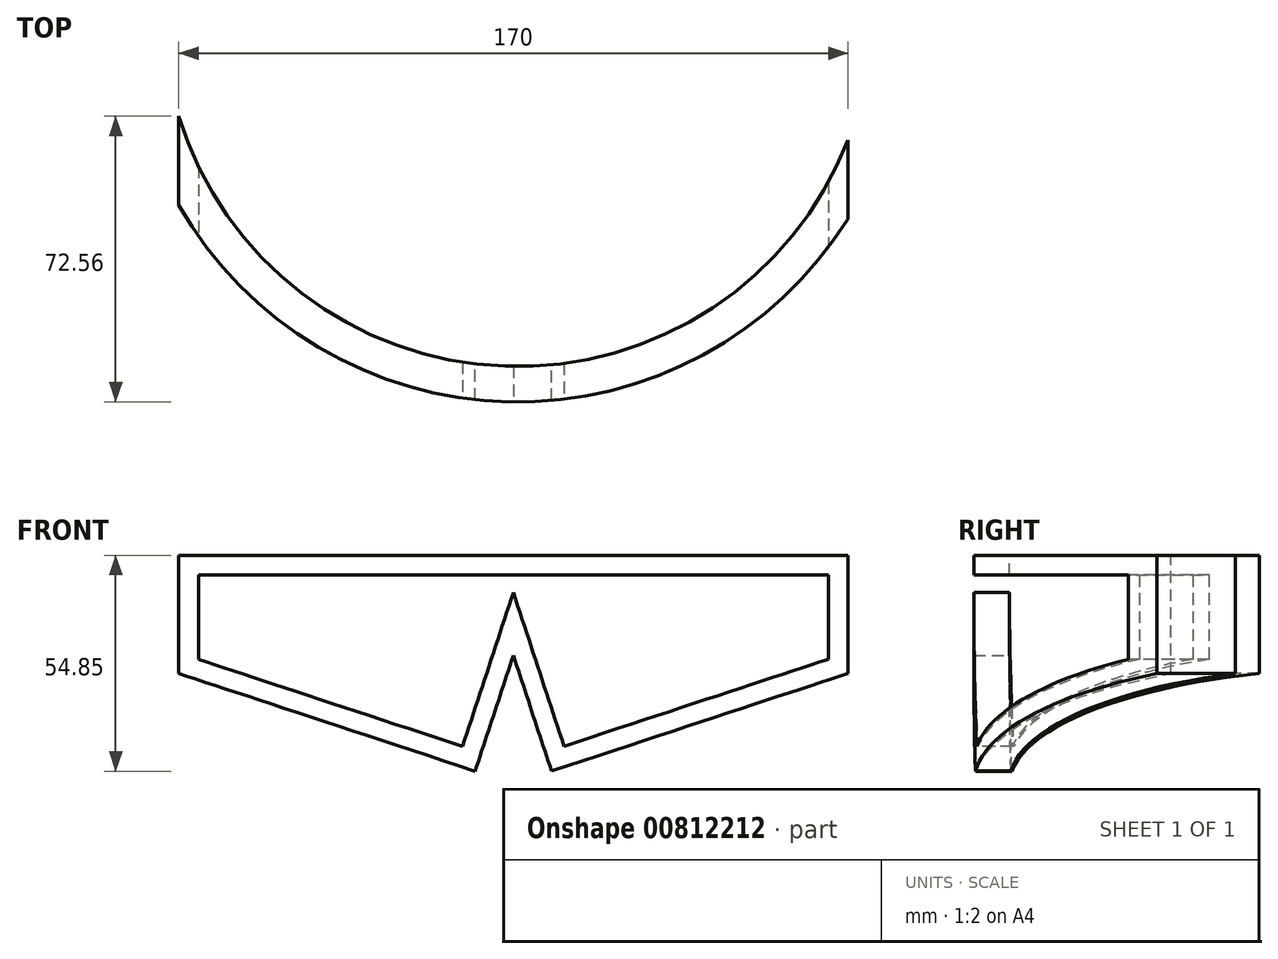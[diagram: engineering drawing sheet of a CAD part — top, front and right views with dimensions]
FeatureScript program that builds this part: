
annotation { "Feature Type Name" : "Feature", "Feature Type Description" : "" }
export const myFeature = defineFeature(function(context is Context, id is Id, definition is map)
    precondition{}
    {
        {
            var Q0;
            Q0=qCreatedBy(makeId("Front.planeOp"),FACE);
            var sketch = newSketch(context, id + "F0", { "sketchPlane" : qUnion([Q0])});
            skLineSegment(sketch, "E0.top", {"start": v(-20.04, 65.04) * mm, "end": v(-105.04, 65.04) * mm});
            skLineSegment(sketch, "E1", {"start": v(-29.75, 10.2) * mm, "end": v(-20.04, 39.64) * mm});
            skLineSegment(sketch, "E2", {"start": v(-29.75, 10.2) * mm, "end": v(-105.04, 35.02) * mm});
            skLineSegment(sketch, "E3", {"start": v(-105.04, 65.04) * mm, "end": v(-105.04, 35.02) * mm});
            skLineSegment(sketch, "E4.MirrorCS", {"start": v(64.96, 65.04) * mm, "end": v(64.96, 35.04) * mm});
            skLineSegment(sketch, "E5.MirrorCS", {"start": v(-10.34, 10.24) * mm, "end": v(64.96, 35.04) * mm});
            skLineSegment(sketch, "E6.MirrorCS", {"start": v(-20.04, 65.04) * mm, "end": v(64.96, 65.04) * mm});
            skLineSegment(sketch, "E7.MirrorCS", {"start": v(-10.34, 10.24) * mm, "end": v(-20.04, 39.64) * mm});
            skSolve(sketch);
        }
        {
            var Q0;
            Q0=makeQuery(id+"F0.imprint","IMPRINT",FACE,{"disambiguationData":[TD([[makeQuery(id+"F0.imprint","IMPRINT",EDGE,{"derivedFrom":sQuery(id+"F0.wireOp",EDGE,"E0.top")}),1.0]])]});
            extrude(context, id + "F1", {"entities" : qUnion([Q0]), "endBound" : BoundingType.SYMMETRIC, "depth" : 150 * mm, "offsetDistance" : 25 * mm});
        }
        {
            var Q0;
            Q0=makeQuery(id+"F1.opExtrude","CAP_FACE",FACE,{"disambiguationData":[OSD([sQuery(id+"F0.wireOp",EDGE,"E0.top"),sQuery(id+"F0.wireOp",EDGE,"E1"),sQuery(id+"F0.wireOp",EDGE,"E2"),sQuery(id+"F0.wireOp",EDGE,"E3"),sQuery(id+"F0.wireOp",EDGE,"E4.MirrorCS"),sQuery(id+"F0.wireOp",EDGE,"E5.MirrorCS"),sQuery(id+"F0.wireOp",EDGE,"E6.MirrorCS"),sQuery(id+"F0.wireOp",EDGE,"E7.MirrorCS")])],"isStart":false});
            var sketch = newSketch(context, id + "F2", { "sketchPlane" : qUnion([Q0])});
            skLineSegment(sketch, "E8.0", {"start": v(-32.93, 16.5) * mm, "end": v(-20.04, 55.6) * mm});
            skLineSegment(sketch, "E8.1", {"start": v(-7.16, 16.55) * mm, "end": v(-20.04, 55.6) * mm});
            skLineSegment(sketch, "E8.2", {"start": v(-100.04, 60.04) * mm, "end": v(-100.04, 38.64) * mm});
            skLineSegment(sketch, "E8.3", {"start": v(-100.04, 60.04) * mm, "end": v(59.96, 60.04) * mm});
            skLineSegment(sketch, "E8.4", {"start": v(59.96, 60.04) * mm, "end": v(59.96, 38.66) * mm});
            skLineSegment(sketch, "E8.5", {"start": v(-32.93, 16.5) * mm, "end": v(-100.04, 38.64) * mm});
            skLineSegment(sketch, "E8.6", {"start": v(-7.16, 16.55) * mm, "end": v(59.96, 38.66) * mm});
            skSolve(sketch);
        }
        {
            var Q0;
            Q0=makeQuery(id+"F1.opExtrude","SWEPT_FACE",FACE,{"disambiguationData":[OSD([sQuery(id+"F0.wireOp",EDGE,"E0.top"),sQuery(id+"F0.wireOp",EDGE,"E6.MirrorCS")])]});
            var sketch = newSketch(context, id + "F3", { "sketchPlane" : qUnion([Q0])});
            skArc(sketch, "E9", {"start": v(-116, 40.66) * mm, "mid": v(-18.98, -38.45) * mm, "end": v(78.03, 40.66) * mm});
            skArc(sketch, "E10.0", {"start": v(-107.18, 42.47) * mm, "mid": v(-18.98, -29.45) * mm, "end": v(69.22, 42.47) * mm});
            skLineSegment(sketch, "E11", {"start": v(-116, 40.66) * mm, "end": v(-107.18, 42.47) * mm});
            skLineSegment(sketch, "E12", {"start": v(69.22, 42.47) * mm, "end": v(78.03, 40.66) * mm});
            skSolve(sketch);
        }
        {
            var Q0;
            Q0=qSketchRegion(id+"F2",true);
            extrude(context, id + "F4", {"entities" : qUnion([Q0]), "operationType" : NewBodyOperationType.REMOVE, "oppositeDirection" : true, "depth" : 200 * mm, "offsetDistance" : 25 * mm});
        }
        {
            var Q0;
            Q0=qSketchRegion(id+"F3",true);
            extrude(context, id + "F5", {"entities" : qUnion([Q0]), "operationType" : NewBodyOperationType.INTERSECT, "oppositeDirection" : true, "depth" : 100 * mm, "offsetDistance" : 25 * mm});
        }
    });
